# Revit family: ПТУ_свайный фундамент
name_source: partatom
category: Специальное оборудование
units: mm (PartAtom-declared; Revit-internal decimal feet)

## family parameters
Всегда вертикально = Нет
На основе рабочей плоскости = Нет
Общий = Нет
При загрузке вырезать с полостями = Нет
Размер круглого соединителя = Использовать диаметр
Тип детали = Нормальный
Точка расчета площади = Нет

## types (8) — shared parameters
ADSK_Единица измерения = шт.
ADSK_Завод-изготовитель = FENSYS
ADSK_Комплект = ПТУ
URL = https://www.fensys.ru
Объём вынимаего грунта = 6.5
zero-valued in all types: Объём бетона

## per-type parameters (varying)
| type | ADSK_Код изделия | ADSK_Масса | ADSK_Наименование | ADSK_Обозначение | Длина стрелы |
| ПТУ со свайным фундаментом., под 6000.,Тёплое исполнение | 53411 | 3400 | Противотаранное устройство с вертикальным подъемом стрелы для остановки т/с массой 3,5 т на скорости 40 км/ч. Перекрываемый проезд 6 м. Электромеханический привод. В комплекте с фундаментом свайной конструкции. Высота стрелы над дорогой - 860 мм. Время закрывания 12 с. Потр. мощность 3 кВт. Температура эксплуатации -20°-+50°. В комплекте: ШУ, пост управления, ф/э безопасности, маячок. | ПТУ-Л 6000ТС | 6000 мм |
| ПТУ со свайным фундаментом., под 6000.,Холодное исполнение | 53403 | 3400 | Противотаранное устройство с вертикальным подъемом стрелы для остановки т/с массой 3,5 т на скорости 40 км/ч. Перекрываемый проезд 6 м. Электромеханический привод. В комплекте с фундаментом свайной конструкции. Высота стрелы над дорогой - 860 мм. Время закрывания 12 с. Потр.мощность 5 кВт. Температура эксплуатации -55°-+50°. В комплекте: ШУ, пост управления, ф/э безопасности, маячок. | ПТУ-Л 6000ХС | 6000 мм |
| ПТУ со свайным фундаментом., под 4000.,Тёплое исполнение | 53408 | 3150 | Противотаранное устройство с вертикальным подъемом стрелы для остановки т/с массой 3,5 т на скорости 40 км/ч. Перекрываемый проезд 4 м. Электромеханический привод. В комплекте с фундаментом свайной конструкции. Высота стрелы над дорогой - 860 мм. Время закрывания 12 с. Потр. мощность 3 кВт. Температура эксплуатации -20°-+50°. В комплекте: ШУ, пост управления, ф/э безопасности, маячок. | ПТУ-Л 4000ТС | 4000 мм |
| ПТУ со свайным фундаментом., под 4000.,Холодное исполнение | 53400 | 3150 | Противотаранное устройство с вертикальным подъемом стрелы для остановки т/с массой 3,5 т на скорости 40 км/ч. Перекрываемый проезд 4 м. Электромеханический привод. В комплекте с фундаментом свайной конструкции. Высота стрелы над дорогой - 860 мм. Время закрывания 12 с. Потр.мощность 5 кВт. Температура эксплуатации -55-+50°. В комплекте: ШУ, пост управления, ф/э безопасности, маячок. | ПТУ-Л 4000ХС | 4000 мм |
| ПТУ со свайным фундаментом., под 4500.,Тёплое исполнение | 53409 | 3200 | Противотаранное устройство с вертикальным подъемом стрелы для остановки т/с массой 3,5 т на скорости 40 км/ч. Перекрываемый проезд 4,5 м. Электромеханический привод. В комплекте с фундаментом свайной конструкции. Высота стрелы над дорогой - 860 мм. Время закрывания 12 с. Потр. мощность 3 кВт. Температура эксплуатации -20°-+50°. В комплекте: ШУ, пост управления, ф/э безопасности, маячок. | ПТУ-Л 4500ТС | 4500 мм |
| ПТУ со свайным фундаментом., под 4500.,Холодное исполнение | 53401 | 3200 | Противотаранное устройство с вертикальным подъемом стрелы для остановки т/с массой 3,5 т на скорости 40 км/ч. Перекрываемый проезд 4,5 м. Электромеханический привод. В комплекте с фундаментом свайной конструкции. Высота стрелы над дорогой - 860 мм. Время закрывания 12 с. Потр.мощность 5 кВт. Температура эксплуатации -55°-+50°. В комплекте: ШУ, пост управления, ф/э безопасности, маячок. | ПТУ-Л 4500ХС | 4500 мм |
| ПТУ со свайным фундаментом., под 5000.,Холодное исполнение | 53402 | 3250 | Противотаранное устройство с вертикальным подъемом стрелы для остановки т/с массой 3,5 т на скорости 40 км/ч. Перекрываемый проезд 5 м. Электромеханический привод. В комплекте с фундаментом свайной конструкции. Высота стрелы над дорогой - 860 мм. Время закрывания 12 с. Потр.мощность 5 кВт. Температура эксплуатации -55°-+50°. В комплекте: ШУ, пост управления, ф/э безопасности, маячок. | ПТУ-Л 5000ХС | 5000 мм |
| ПТУ со свайным фундаментом., под 5000.,Тёплое исполнение | 53410 | 3250 | Противотаранное устройство с вертикальным подъемом стрелы для остановки т/с массой 3,5 т на скорости 40 км/ч. Перекрываемый проезд 5 м. Электромеханический привод. В комплекте с фундаментом свайной конструкции. Высота стрелы над дорогой - 860 мм. Время закрывания 12 с. Потр. мощность 3 кВт. Температура эксплуатации -20°-+50°. В комплекте: ШУ, пост управления, ф/э безопасности, маячок. | ПТУ-Л 5000ТС | 5000 мм |
